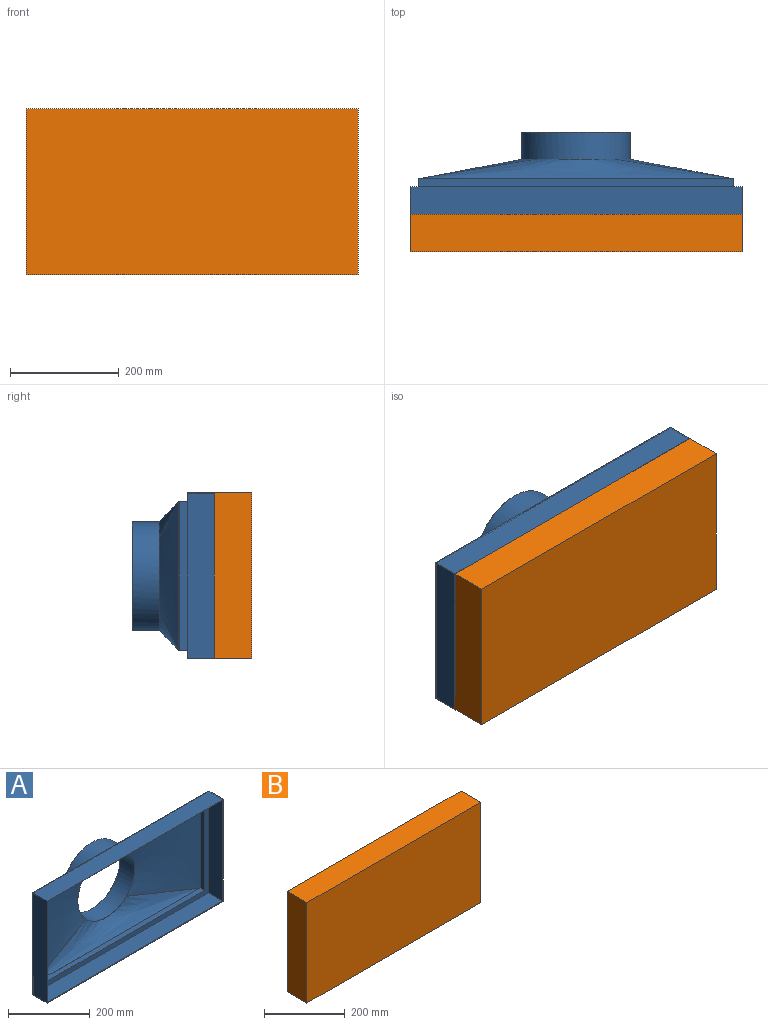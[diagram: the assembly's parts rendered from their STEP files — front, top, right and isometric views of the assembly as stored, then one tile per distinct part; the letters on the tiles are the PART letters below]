
ASSEMBLY  parts=2 mates=1
PART A: 30 faces, bbox 613x154x308 mm
  f0: plane 610x305mm, normal (0,1,0), area 26550mm2, adj f1,f2,f3,f4,f6,f7,f8,f9
  f1: plane 305x50mm, normal (1,0,0), area 15250mm2, adj f0,f2,f4,f5
  f2: plane 610x50mm, normal (0,0,-1), area 30500mm2, adj f0,f1,f3,f5
  f3: plane 305x50mm, normal (-1,0,0), area 15250mm2, adj f0,f2,f4,f5
  f4: plane 610x50mm, normal (0,0,1), area 30500mm2, adj f0,f1,f3,f5
  f5: plane 610x305mm, normal (0,-1,0), area 2736mm2, adj f1,f2,f3,f4,f17,f18,f19,f20
  f6: plane 580x15mm, normal (0,0,1), area 8700mm2, adj f0,f7,f9,f13
  f7: plane 275x15mm, normal (1,0,0), area 4125mm2, adj f0,f6,f8,f12
  f8: plane 580x15mm, normal (0,0,-1), area 8700mm2, adj f0,f7,f9,f15
  f9: plane 275x15mm, normal (-1,0,0), area 4125mm2, adj f0,f6,f8,f14
  f10: cylinder r=100mm len=200mm, axis (0,1,0), area 31415.9mm2, adj f11,f12,f13,f14,f15
  f11: plane 200x200mm, normal (0,1,0), area 935.4mm2, adj f10,f25
  f12: bspline ~277.75x220.4mm, area 43485mm2, adj f7,f10,f13,f15
  f13: bspline ~585.8x69.17mm, area 25259.3mm2, adj f6,f10,f12,f14
  f14: bspline ~277.75x220.4mm, area 43485mm2, adj f9,f10,f13,f15
  f15: bspline ~585.8x69.17mm, area 25259.3mm2, adj f8,f10,f12,f14
  f16: plane 607x302mm, normal (0,-1,0), area 26370mm2, adj f17,f18,f19,f20,f21,f22,f23,f24
  f17: plane 302x48.5mm, normal (-1,0,0), area 14647mm2, adj f5,f16,f18,f20
  f18: plane 607x48.5mm, normal (0,0,1), area 29439.5mm2, adj f5,f16,f17,f19
  f19: plane 302x48.5mm, normal (1,0,0), area 14647mm2, adj f5,f16,f18,f20
  f20: plane 607x48.5mm, normal (0,0,-1), area 29439.5mm2, adj f5,f16,f17,f19
  f21: plane 577.11x15.97mm, normal (0,0,-1), area 9093.9mm2, adj f16,f22,f24,f26,f27,f28
  f22: plane 272.26x15.52mm, normal (-1,0,0), area 4147mm2, adj f16,f21,f23,f26
  f23: plane 577.11x15.97mm, normal (0,0,1), area 9093.9mm2, adj f16,f22,f24,f26,f28,f29
  f24: plane 272.26x15.52mm, normal (1,0,0), area 4147mm2, adj f16,f21,f23,f28
  f25: cylinder r=98.5mm len=197mm, axis (0,1,0), area 31631.6mm2, adj f11,f26,f27,f28,f29
  f26: offset ~283.5x226.14mm, area 43241.2mm2, adj f21,f22,f23,f25,f27,f29
  f27: offset ~594.6x72.17mm, area 24601.8mm2, adj f21,f25,f26,f28
  f28: offset ~283.5x226.14mm, area 43241.2mm2, adj f21,f23,f24,f25,f27,f29
  f29: offset ~594.6x72.17mm, area 24601.8mm2, adj f23,f25,f26,f28
PART B: 6 faces, bbox 610x69x305 mm
  f0: plane 610x69mm, normal (0,0,-1), area 42090mm2, adj f1,f3,f4,f5
  f1: plane 305x69mm, normal (1,0,0), area 21045mm2, adj f0,f2,f4,f5
  f2: plane 610x69mm, normal (0,0,1), area 42090mm2, adj f1,f3,f4,f5
  f3: plane 305x69mm, normal (-1,0,0), area 21045mm2, adj f0,f2,f4,f5
  f4: plane 610x305mm, normal (0,1,0), area 186050mm2, adj f0,f1,f2,f3
  f5: plane 610x305mm, normal (0,-1,0), area 186050mm2, adj f0,f1,f2,f3
PLACE A at identity
PLACE B at identity fixed
MATE fastened A.f5 <-> B.f4  axis (0,-1,0) through (305,69,152.5)mm
